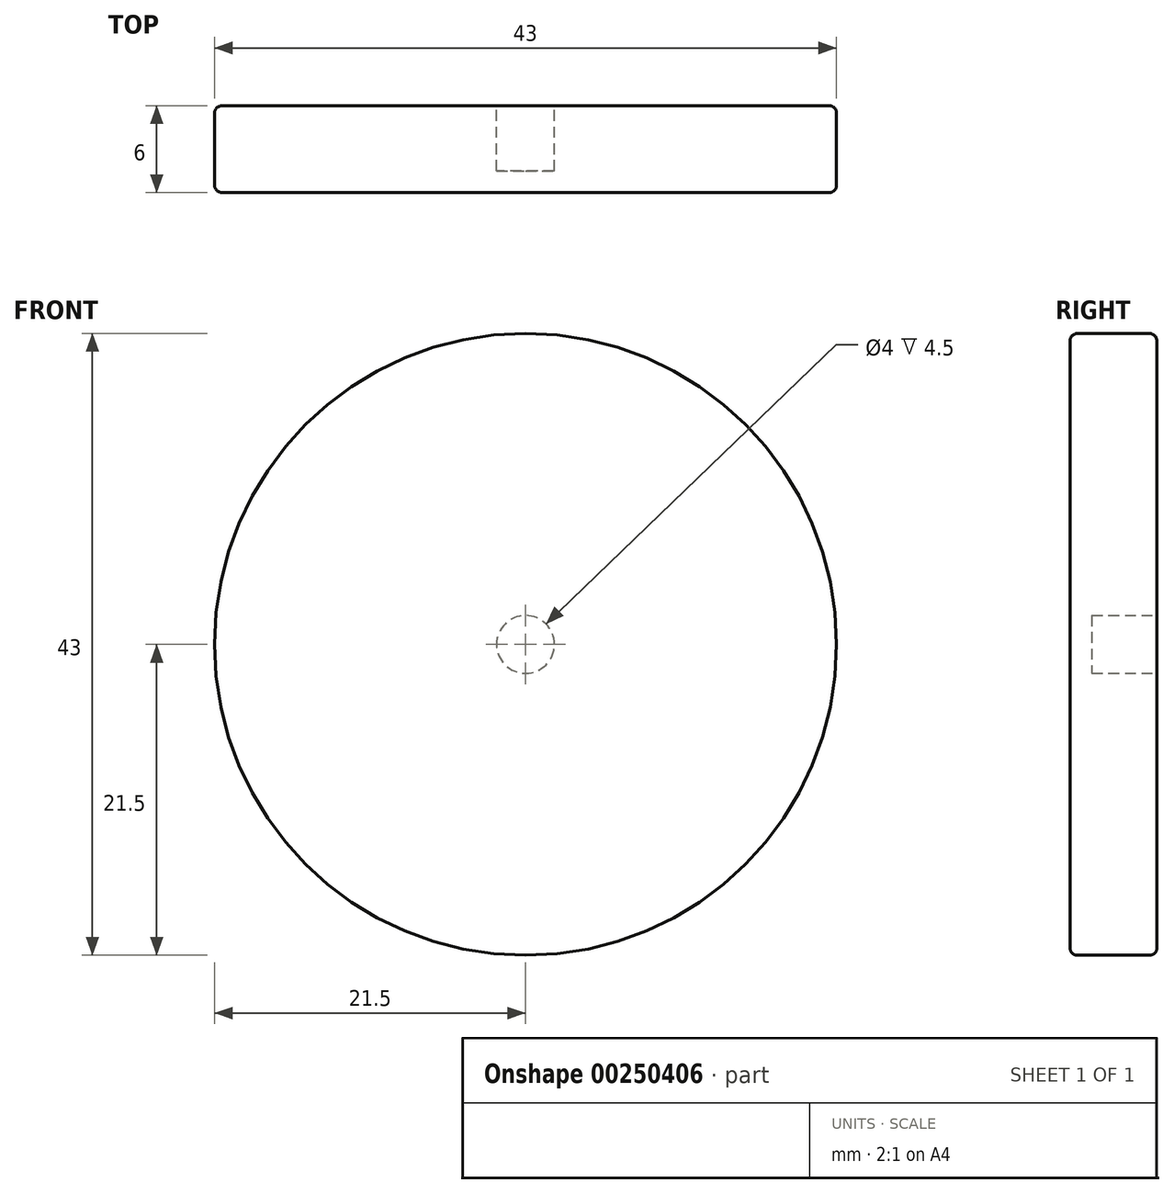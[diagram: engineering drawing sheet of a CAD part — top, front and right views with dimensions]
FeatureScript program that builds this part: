
annotation { "Feature Type Name" : "Feature", "Feature Type Description" : "" }
export const myFeature = defineFeature(function(context is Context, id is Id, definition is map)
    precondition{}
    {
        {
            var Q0;
            Q0=qCreatedBy(makeId("Front.planeOp"),FACE);
            var sketch = newSketch(context, id + "F0", { "sketchPlane" : qUnion([Q0])});
            skCircle(sketch, "E0", {"center": v(0, 0) * mm, "radius": 21.5 * mm});
            skSolve(sketch);
        }
        {
            var Q0;
            Q0 = qSketchRegion(id + "F0", true);
            extrude(context, id + "F1", {"entities" : qUnion([Q0]), "depth" : 6 * mm});
        }
        {
            var Q0;
            Q0=makeQuery(id+"F1.opExtrude","CAP_FACE",FACE,{"disambiguationData":[OSD([sQuery(id+"F0.wireOp",EDGE,"E0")])],"isStart":true});
            var sketch = newSketch(context, id + "F2", { "sketchPlane" : qUnion([Q0])});
            skCircle(sketch, "E1", {"center": v(0, 0) * mm, "radius": 2 * mm});
            skSolve(sketch);
        }
        {
            var Q0;
            Q0 = qSketchRegion(id + "F2", true);
            extrude(context, id + "F3", {"entities" : qUnion([Q0]), "operationType" : NewBodyOperationType.REMOVE, "oppositeDirection" : true, "depth" : 4.5 * mm});
        }
        {
            var Q0;
            Q0=makeQuery(id+"F1.opExtrude","CAP_EDGE",EDGE,{"disambiguationData":[OSD([sQuery(id+"F0.wireOp",EDGE,"E0")])],"isStart":true});
            var Q1;
            Q1=makeQuery(id+"F1.opExtrude","CAP_EDGE",EDGE,{"disambiguationData":[OSD([sQuery(id+"F0.wireOp",EDGE,"E0")])],"isStart":false});
            fillet(context, id + "F4", {"entities" : qUnion([Q0, Q1]), "radius" : .5 * mm, "tangentPropagation" : true, "allowEdgeOverflow" : false});
        }
    });
